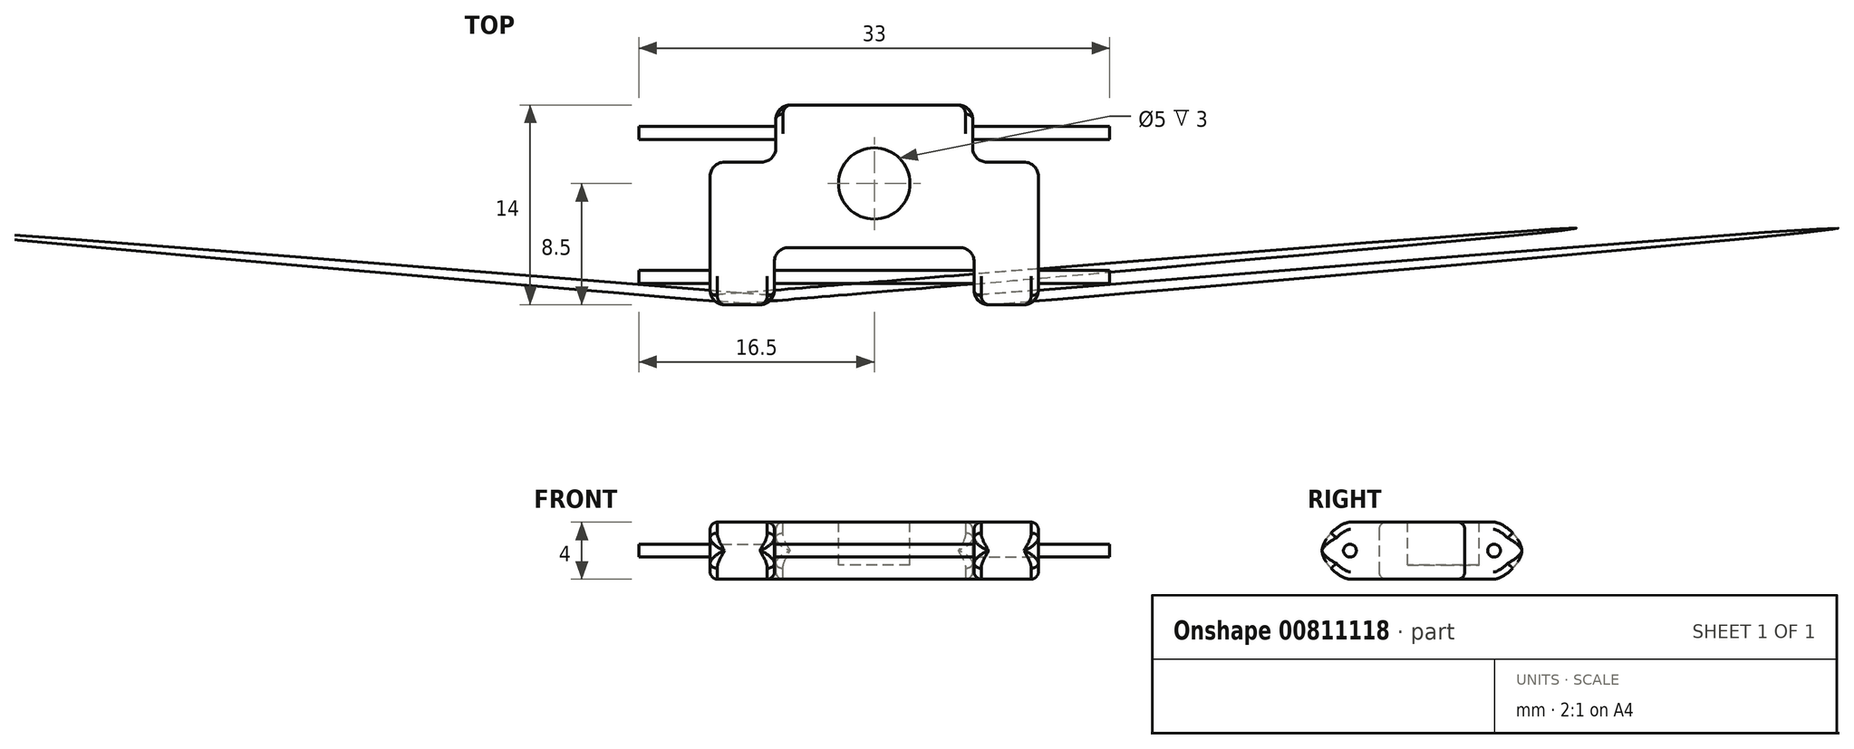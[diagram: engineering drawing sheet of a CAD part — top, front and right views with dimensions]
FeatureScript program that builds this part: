
annotation { "Feature Type Name" : "Feature", "Feature Type Description" : "" }
export const myFeature = defineFeature(function(context is Context, id is Id, definition is map)
    precondition{}
    {
        {
            var Q0;
            Q0=qCreatedBy(makeId("Top.planeOp"),FACE);
            var sketch = newSketch(context, id + "F0", { "sketchPlane" : qUnion([Q0])});
            skLineSegment(sketch, "E0", {"start": v(-1, -14) * mm, "end": v(-1, -10) * mm});
            skLineSegment(sketch, "E1", {"start": v(-1, -10) * mm, "end": v(-15, -10) * mm});
            skLineSegment(sketch, "E2", {"start": v(-15, -10) * mm, "end": v(-15, -14) * mm});
            skLineSegment(sketch, "E3", {"start": v(-15, -14) * mm, "end": v(-19.5, -14) * mm});
            skLineSegment(sketch, "E4", {"start": v(-1, -14) * mm, "end": v(3.5, -14) * mm});
            skLineSegment(sketch, "E5", {"start": v(-19.5, -14) * mm, "end": v(-19.5, -4) * mm});
            skLineSegment(sketch, "E6", {"start": v(-19.5, -4) * mm, "end": v(-14.9, -4) * mm});
            skLineSegment(sketch, "E7", {"start": v(-14.9, -4) * mm, "end": v(-14.9, 0) * mm});
            skLineSegment(sketch, "E8", {"start": v(-14.9, 0) * mm, "end": v(-1.1, 0) * mm});
            skLineSegment(sketch, "E9", {"start": v(-1.1, 0) * mm, "end": v(-1.1, -4) * mm});
            skLineSegment(sketch, "E10", {"start": v(-1.1, -4) * mm, "end": v(3.5, -4) * mm});
            skLineSegment(sketch, "E11", {"start": v(3.5, -4) * mm, "end": v(3.5, -14) * mm});
            skSolve(sketch);
        }
        {
            var Q0;
            Q0=makeQuery(id+"F0.imprint","IMPRINT",FACE,{"disambiguationData":[TD([[makeQuery(id+"F0.imprint","IMPRINT",EDGE,{"derivedFrom":sQuery(id+"F0.wireOp",EDGE,"E0")}),-1.0]])]});
            extrude(context, id + "F1", {"entities" : qUnion([Q0]), "depth" : 4 * mm, "offsetDistance" : 25 * mm});
        }
        {
            var Q0;
            Q0=makeQuery(id+"F1.opExtrude","SWEPT_EDGE",EDGE,{"disambiguationData":[OSD([sQuery(id+"F0.wireOp",EDGE,"JVpa2NSN-jCbz-SYZh-2br0-VPJ9OqO5sEDm"),sQuery(id+"F0.wireOp",EDGE,"TmuEh8Bb-qYGH-lmF9-es9h-PXmLGTj7apYS")])]});
            var Q1;
            Q1=makeQuery(id+"F1.opExtrude","SWEPT_EDGE",EDGE,{"disambiguationData":[OSD([sQuery(id+"F0.wireOp",EDGE,"Ta08JTOG-JjW1-DyQu-Rjfl-olB2hLuTZKrI"),sQuery(id+"F0.wireOp",EDGE,"5RLxsvr7-zWRq-nJ0O-23qe-XEgADmnkmLba")])]});
            var Q2;
            Q2=makeQuery(id+"F1.opExtrude","SWEPT_EDGE",EDGE,{"disambiguationData":[OSD([sQuery(id+"F0.wireOp",EDGE,"JVpa2NSN-jCbz-SYZh-2br0-VPJ9OqO5sEDm"),sQuery(id+"F0.wireOp",EDGE,"iIMMWLLX-5pRk-kAWc-YyXh-X3XYjQtiHgF8")])]});
            var Q3;
            Q3=makeQuery(id+"F1.opExtrude","SWEPT_EDGE",EDGE,{"disambiguationData":[OSD([sQuery(id+"F0.wireOp",EDGE,"Bp2VUUx9-f2Nf-Cqm2-FavC-f2X54JljXIIN"),sQuery(id+"F0.wireOp",EDGE,"TmuEh8Bb-qYGH-lmF9-es9h-PXmLGTj7apYS")])]});
            var Q4;
            Q4=makeQuery(id+"F1.opExtrude","SWEPT_EDGE",EDGE,{"disambiguationData":[OSD([sQuery(id+"F0.wireOp",EDGE,"aM0JYdi9-BpOH-c1Sx-eQZ7-4LdQcpM627Qa"),sQuery(id+"F0.wireOp",EDGE,"Ta08JTOG-JjW1-DyQu-Rjfl-olB2hLuTZKrI")])]});
            var Q5;
            Q5=makeQuery(id+"F1.opExtrude","SWEPT_EDGE",EDGE,{"disambiguationData":[OSD([sQuery(id+"F0.wireOp",EDGE,"5RLxsvr7-zWRq-nJ0O-23qe-XEgADmnkmLba"),sQuery(id+"F0.wireOp",EDGE,"Bp2VUUx9-f2Nf-Cqm2-FavC-f2X54JljXIIN")])]});
            var Q6;
            Q6=makeQuery(id+"F1.opExtrude","SWEPT_EDGE",EDGE,{"disambiguationData":[OSD([sQuery(id+"F0.wireOp",EDGE,"yeDMJLls-6pq1-5wso-vwFU-Q73Pk40JU32b"),sQuery(id+"F0.wireOp",EDGE,"aM0JYdi9-BpOH-c1Sx-eQZ7-4LdQcpM627Qa")])]});
            var Q7;
            Q7=makeQuery(id+"F1.opExtrude","SWEPT_EDGE",EDGE,{"disambiguationData":[OSD([sQuery(id+"F0.wireOp",EDGE,"yeDMJLls-6pq1-5wso-vwFU-Q73Pk40JU32b"),sQuery(id+"F0.wireOp",EDGE,"oADVPvip-QRiO-k2je-1GcM-0gCGYZzCVpqe")])]});
            var Q8;
            Q8=makeQuery(id+"F1.opExtrude","SWEPT_EDGE",EDGE,{"disambiguationData":[OSD([sQuery(id+"F0.wireOp",EDGE,"oADVPvip-QRiO-k2je-1GcM-0gCGYZzCVpqe"),sQuery(id+"F0.wireOp",EDGE,"10rlgXVg-n50c-kqx7-uExC-2RYqwfv1c7cX")])]});
            var Q9;
            Q9=makeQuery(id+"F1.opExtrude","SWEPT_EDGE",EDGE,{"disambiguationData":[OSD([sQuery(id+"F0.wireOp",EDGE,"TUznSBm0-cCe5-ovrQ-pSbA-vPagOil4q95r"),sQuery(id+"F0.wireOp",EDGE,"10rlgXVg-n50c-kqx7-uExC-2RYqwfv1c7cX")])]});
            var Q10;
            Q10=makeQuery(id+"F1.opExtrude","SWEPT_EDGE",EDGE,{"disambiguationData":[OSD([sQuery(id+"F0.wireOp",EDGE,"dIuJsfEi-w8Eu-UMFV-xWrQ-Q2fZL97E1xqK"),sQuery(id+"F0.wireOp",EDGE,"TUznSBm0-cCe5-ovrQ-pSbA-vPagOil4q95r")])]});
            var Q11;
            Q11=makeQuery(id+"F1.opExtrude","SWEPT_EDGE",EDGE,{"disambiguationData":[OSD([sQuery(id+"F0.wireOp",EDGE,"iIMMWLLX-5pRk-kAWc-YyXh-X3XYjQtiHgF8"),sQuery(id+"F0.wireOp",EDGE,"dIuJsfEi-w8Eu-UMFV-xWrQ-Q2fZL97E1xqK")])]});
            var Q12;
            Q12=makeQuery(id+"F1.opExtrude","SWEPT_EDGE",EDGE,{"disambiguationData":[OSD([sQuery(id+"F0.wireOp",EDGE,"yLF3BCVI-Jb2U-5dZP-aiB0-7200LCA53yiJ"),sQuery(id+"F0.wireOp",EDGE,"E3")])]});
            var Q13;
            Q13=makeQuery(id+"F1.opExtrude","SWEPT_EDGE",EDGE,{"disambiguationData":[OSD([sQuery(id+"F0.wireOp",EDGE,"E2"),sQuery(id+"F0.wireOp",EDGE,"E3")])]});
            var Q14;
            Q14=makeQuery(id+"F1.opExtrude","SWEPT_EDGE",EDGE,{"disambiguationData":[OSD([sQuery(id+"F0.wireOp",EDGE,"E1"),sQuery(id+"F0.wireOp",EDGE,"E2")])]});
            var Q15;
            Q15=makeQuery(id+"F1.opExtrude","SWEPT_EDGE",EDGE,{"disambiguationData":[OSD([sQuery(id+"F0.wireOp",EDGE,"E0"),sQuery(id+"F0.wireOp",EDGE,"E1")])]});
            var Q16;
            Q16=makeQuery(id+"F1.opExtrude","SWEPT_EDGE",EDGE,{"disambiguationData":[OSD([sQuery(id+"F0.wireOp",EDGE,"E0"),sQuery(id+"F0.wireOp",EDGE,"E4")])]});
            var Q17;
            Q17=makeQuery(id+"F1.opExtrude","SWEPT_EDGE",EDGE,{"disambiguationData":[OSD([sQuery(id+"F0.wireOp",EDGE,"W0sLsfjq-YAJu-qSV0-cM3q-n6XLMPe2tytr"),sQuery(id+"F0.wireOp",EDGE,"E4")])]});
            var Q18;
            Q18=makeQuery(id+"F1.opExtrude","SWEPT_EDGE",EDGE,{"disambiguationData":[OSD([sQuery(id+"F0.wireOp",EDGE,"E5"),sQuery(id+"F0.wireOp",EDGE,"E6")])]});
            var Q19;
            Q19=makeQuery(id+"F1.opExtrude","SWEPT_EDGE",EDGE,{"disambiguationData":[OSD([sQuery(id+"F0.wireOp",EDGE,"E6"),sQuery(id+"F0.wireOp",EDGE,"E7")])]});
            var Q20;
            Q20=makeQuery(id+"F1.opExtrude","SWEPT_EDGE",EDGE,{"disambiguationData":[OSD([sQuery(id+"F0.wireOp",EDGE,"E7"),sQuery(id+"F0.wireOp",EDGE,"E8")])]});
            var Q21;
            Q21=makeQuery(id+"F1.opExtrude","SWEPT_EDGE",EDGE,{"disambiguationData":[OSD([sQuery(id+"F0.wireOp",EDGE,"E8"),sQuery(id+"F0.wireOp",EDGE,"E9")])]});
            var Q22;
            Q22=makeQuery(id+"F1.opExtrude","SWEPT_EDGE",EDGE,{"disambiguationData":[OSD([sQuery(id+"F0.wireOp",EDGE,"E9"),sQuery(id+"F0.wireOp",EDGE,"E10")])]});
            var Q23;
            Q23=makeQuery(id+"F1.opExtrude","SWEPT_EDGE",EDGE,{"disambiguationData":[OSD([sQuery(id+"F0.wireOp",EDGE,"E10"),sQuery(id+"F0.wireOp",EDGE,"E11")])]});
            fillet(context, id + "F2", {"entities" : qUnion([Q0, Q1, Q2, Q3, Q4, Q5, Q6, Q7, Q8, Q9, Q10, Q11, Q12, Q13, Q14, Q15, Q16, Q17, Q18, Q19, Q20, Q21, Q22, Q23]), "radius" : 1 * mm, "tangentPropagation" : true, "allowEdgeOverflow" : false});
        }
        {
            var Q0;
            Q0=makeQuery(id+"F1.opExtrude","CAP_EDGE",EDGE,{"disambiguationData":[OSD([sQuery(id+"F0.wireOp",EDGE,"E8")])],"isStart":true});
            var Q1;
            Q1=makeQuery(id+"F1.opExtrude","CAP_EDGE",EDGE,{"disambiguationData":[OSD([sQuery(id+"F0.wireOp",EDGE,"E8")])],"isStart":false});
            var Q2;
            Q2=makeQuery(id+"F1.opExtrude","CAP_EDGE",EDGE,{"disambiguationData":[OSD([sQuery(id+"F0.wireOp",EDGE,"E3")])],"isStart":true});
            var Q3;
            Q3=makeQuery(id+"F1.opExtrude","CAP_EDGE",EDGE,{"disambiguationData":[OSD([sQuery(id+"F0.wireOp",EDGE,"E3")])],"isStart":false});
            var Q4;
            Q4=makeQuery(id+"F1.opExtrude","CAP_EDGE",EDGE,{"disambiguationData":[OSD([sQuery(id+"F0.wireOp",EDGE,"E4")])],"isStart":false});
            var Q5;
            Q5=makeQuery(id+"F1.opExtrude","CAP_EDGE",EDGE,{"disambiguationData":[OSD([sQuery(id+"F0.wireOp",EDGE,"E4")])],"isStart":true});
            fillet(context, id + "F3", {"entities" : qUnion([Q0, Q1, Q2, Q3, Q4, Q5]), "radius" : 2 * mm, "rho" : 0.3, "crossSection" : FilletCrossSection.CONIC, "allowEdgeOverflow" : false});
        }
        {
            var Q0;
            Q0=makeQuery(id+"F1.opExtrude","CAP_EDGE",EDGE,{"disambiguationData":[OSD([sQuery(id+"F0.wireOp",EDGE,"E1")])],"isStart":true});
            var Q1;
            {var subQ0=sQuery(id+"F0.wireOp",EDGE,"E2");var subQ1=sQuery(id+"F0.wireOp",EDGE,"E1");Q1=makeQuery(id+"F2.opFillet","BLEND_EDGE",EDGE,{"blendedFrom":[makeQuery(id+"F1.opExtrude","SWEPT_EDGE",EDGE,{"disambiguationData":[OSD([subQ1,subQ0])]}),makeQuery(id+"F1.opExtrude","CAP_FACE",FACE,{"disambiguationData":[OSD([sQuery(id+"F0.wireOp",EDGE,"E0"),subQ1,subQ0,sQuery(id+"F0.wireOp",EDGE,"E3"),sQuery(id+"F0.wireOp",EDGE,"E4"),sQuery(id+"F0.wireOp",EDGE,"E5"),sQuery(id+"F0.wireOp",EDGE,"E6"),sQuery(id+"F0.wireOp",EDGE,"E7"),sQuery(id+"F0.wireOp",EDGE,"E8"),sQuery(id+"F0.wireOp",EDGE,"E9"),sQuery(id+"F0.wireOp",EDGE,"E10"),sQuery(id+"F0.wireOp",EDGE,"E11")])],"isStart":true})],"blendedInto":[makeQuery(id+"F1.opExtrude","CAP_FACE",FACE,{"disambiguationData":[OSD([sQuery(id+"F0.wireOp",EDGE,"E0"),subQ1,subQ0,sQuery(id+"F0.wireOp",EDGE,"E3"),sQuery(id+"F0.wireOp",EDGE,"E4"),sQuery(id+"F0.wireOp",EDGE,"E5"),sQuery(id+"F0.wireOp",EDGE,"E6"),sQuery(id+"F0.wireOp",EDGE,"E7"),sQuery(id+"F0.wireOp",EDGE,"E8"),sQuery(id+"F0.wireOp",EDGE,"E9"),sQuery(id+"F0.wireOp",EDGE,"E10"),sQuery(id+"F0.wireOp",EDGE,"E11")])],"isStart":true})]});}
            var Q2;
            Q2=makeQuery(id+"F1.opExtrude","CAP_EDGE",EDGE,{"disambiguationData":[OSD([sQuery(id+"F0.wireOp",EDGE,"E2")])],"isStart":true});
            var Q3;
            Q3=makeQuery(id+"F3.opFillet","BLEND_EDGE",EDGE,{"blendedFrom":[makeQuery(id+"F1.opExtrude","CAP_EDGE",EDGE,{"disambiguationData":[OSD([sQuery(id+"F0.wireOp",EDGE,"E3")])],"isStart":true}),makeQuery(id+"F1.opExtrude","SWEPT_FACE",FACE,{"disambiguationData":[OSD([sQuery(id+"F0.wireOp",EDGE,"E2")])]})],"blendedInto":[makeQuery(id+"F1.opExtrude","SWEPT_FACE",FACE,{"disambiguationData":[OSD([sQuery(id+"F0.wireOp",EDGE,"E2")])]})]});
            var Q4;
            {var subQ0=sQuery(id+"F0.wireOp",EDGE,"E3");Q4=makeQuery(id+"F3.opFillet","BLEND_EDGE",EDGE,{"blendedFrom":[makeQuery(id+"F1.opExtrude","CAP_EDGE",EDGE,{"disambiguationData":[OSD([subQ0])],"isStart":true}),makeQuery(id+"F2.opFillet","BLEND_FACE",FACE,{"disambiguationData":[OSD([sQuery(id+"F0.wireOp",EDGE,"E2"),subQ0])]})],"blendedInto":[makeQuery(id+"F2.opFillet","BLEND_FACE",FACE,{"disambiguationData":[OSD([sQuery(id+"F0.wireOp",EDGE,"E2"),subQ0])]})]});}
            var Q5;
            {var subQ0=sQuery(id+"F0.wireOp",EDGE,"E1");var subQ1=sQuery(id+"F0.wireOp",EDGE,"E0");Q5=makeQuery(id+"F2.opFillet","BLEND_EDGE",EDGE,{"blendedFrom":[makeQuery(id+"F1.opExtrude","SWEPT_EDGE",EDGE,{"disambiguationData":[OSD([subQ1,subQ0])]}),makeQuery(id+"F1.opExtrude","CAP_FACE",FACE,{"disambiguationData":[OSD([subQ1,subQ0,sQuery(id+"F0.wireOp",EDGE,"E2"),sQuery(id+"F0.wireOp",EDGE,"E3"),sQuery(id+"F0.wireOp",EDGE,"E4"),sQuery(id+"F0.wireOp",EDGE,"E5"),sQuery(id+"F0.wireOp",EDGE,"E6"),sQuery(id+"F0.wireOp",EDGE,"E7"),sQuery(id+"F0.wireOp",EDGE,"E8"),sQuery(id+"F0.wireOp",EDGE,"E9"),sQuery(id+"F0.wireOp",EDGE,"E10"),sQuery(id+"F0.wireOp",EDGE,"E11")])],"isStart":true})],"blendedInto":[makeQuery(id+"F1.opExtrude","CAP_FACE",FACE,{"disambiguationData":[OSD([subQ1,subQ0,sQuery(id+"F0.wireOp",EDGE,"E2"),sQuery(id+"F0.wireOp",EDGE,"E3"),sQuery(id+"F0.wireOp",EDGE,"E4"),sQuery(id+"F0.wireOp",EDGE,"E5"),sQuery(id+"F0.wireOp",EDGE,"E6"),sQuery(id+"F0.wireOp",EDGE,"E7"),sQuery(id+"F0.wireOp",EDGE,"E8"),sQuery(id+"F0.wireOp",EDGE,"E9"),sQuery(id+"F0.wireOp",EDGE,"E10"),sQuery(id+"F0.wireOp",EDGE,"E11")])],"isStart":true})]});}
            var Q6;
            Q6=makeQuery(id+"F1.opExtrude","CAP_EDGE",EDGE,{"disambiguationData":[OSD([sQuery(id+"F0.wireOp",EDGE,"E0")])],"isStart":true});
            var Q7;
            {var subQ0=sQuery(id+"F0.wireOp",EDGE,"E4");Q7=makeQuery(id+"F3.opFillet","BLEND_EDGE",EDGE,{"blendedFrom":[makeQuery(id+"F1.opExtrude","CAP_EDGE",EDGE,{"disambiguationData":[OSD([subQ0])],"isStart":true}),makeQuery(id+"F2.opFillet","BLEND_FACE",FACE,{"disambiguationData":[OSD([sQuery(id+"F0.wireOp",EDGE,"E0"),subQ0])]})],"blendedInto":[makeQuery(id+"F2.opFillet","BLEND_FACE",FACE,{"disambiguationData":[OSD([sQuery(id+"F0.wireOp",EDGE,"E0"),subQ0])]})]});}
            var Q8;
            {var subQ0=sQuery(id+"F0.wireOp",EDGE,"E4");Q8=makeQuery(id+"F3.opFillet","BLEND_EDGE",EDGE,{"blendedFrom":[makeQuery(id+"F1.opExtrude","CAP_EDGE",EDGE,{"disambiguationData":[OSD([subQ0])],"isStart":false}),makeQuery(id+"F2.opFillet","BLEND_FACE",FACE,{"disambiguationData":[OSD([sQuery(id+"F0.wireOp",EDGE,"E0"),subQ0])]})],"blendedInto":[makeQuery(id+"F2.opFillet","BLEND_FACE",FACE,{"disambiguationData":[OSD([sQuery(id+"F0.wireOp",EDGE,"E0"),subQ0])]})]});}
            var Q9;
            {var subQ0=sQuery(id+"F0.wireOp",EDGE,"E3");Q9=makeQuery(id+"F3.opFillet","BLEND_EDGE",EDGE,{"blendedFrom":[makeQuery(id+"F1.opExtrude","CAP_EDGE",EDGE,{"disambiguationData":[OSD([subQ0])],"isStart":false}),makeQuery(id+"F2.opFillet","BLEND_FACE",FACE,{"disambiguationData":[OSD([sQuery(id+"F0.wireOp",EDGE,"E2"),subQ0])]})],"blendedInto":[makeQuery(id+"F2.opFillet","BLEND_FACE",FACE,{"disambiguationData":[OSD([sQuery(id+"F0.wireOp",EDGE,"E2"),subQ0])]})]});}
            var Q10;
            Q10=makeQuery(id+"F3.opFillet","BLEND_EDGE",EDGE,{"blendedFrom":[makeQuery(id+"F1.opExtrude","CAP_EDGE",EDGE,{"disambiguationData":[OSD([sQuery(id+"F0.wireOp",EDGE,"E3")])],"isStart":false}),makeQuery(id+"F1.opExtrude","SWEPT_FACE",FACE,{"disambiguationData":[OSD([sQuery(id+"F0.wireOp",EDGE,"E2")])]})],"blendedInto":[makeQuery(id+"F1.opExtrude","SWEPT_FACE",FACE,{"disambiguationData":[OSD([sQuery(id+"F0.wireOp",EDGE,"E2")])]})]});
            var Q11;
            Q11=makeQuery(id+"F1.opExtrude","CAP_EDGE",EDGE,{"disambiguationData":[OSD([sQuery(id+"F0.wireOp",EDGE,"E2")])],"isStart":false});
            var Q12;
            {var subQ0=sQuery(id+"F0.wireOp",EDGE,"E2");var subQ1=sQuery(id+"F0.wireOp",EDGE,"E1");Q12=makeQuery(id+"F2.opFillet","BLEND_EDGE",EDGE,{"blendedFrom":[makeQuery(id+"F1.opExtrude","SWEPT_EDGE",EDGE,{"disambiguationData":[OSD([subQ1,subQ0])]}),makeQuery(id+"F1.opExtrude","CAP_FACE",FACE,{"disambiguationData":[OSD([sQuery(id+"F0.wireOp",EDGE,"E0"),subQ1,subQ0,sQuery(id+"F0.wireOp",EDGE,"E3"),sQuery(id+"F0.wireOp",EDGE,"E4"),sQuery(id+"F0.wireOp",EDGE,"E5"),sQuery(id+"F0.wireOp",EDGE,"E6"),sQuery(id+"F0.wireOp",EDGE,"E7"),sQuery(id+"F0.wireOp",EDGE,"E8"),sQuery(id+"F0.wireOp",EDGE,"E9"),sQuery(id+"F0.wireOp",EDGE,"E10"),sQuery(id+"F0.wireOp",EDGE,"E11")])],"isStart":false})],"blendedInto":[makeQuery(id+"F1.opExtrude","CAP_FACE",FACE,{"disambiguationData":[OSD([sQuery(id+"F0.wireOp",EDGE,"E0"),subQ1,subQ0,sQuery(id+"F0.wireOp",EDGE,"E3"),sQuery(id+"F0.wireOp",EDGE,"E4"),sQuery(id+"F0.wireOp",EDGE,"E5"),sQuery(id+"F0.wireOp",EDGE,"E6"),sQuery(id+"F0.wireOp",EDGE,"E7"),sQuery(id+"F0.wireOp",EDGE,"E8"),sQuery(id+"F0.wireOp",EDGE,"E9"),sQuery(id+"F0.wireOp",EDGE,"E10"),sQuery(id+"F0.wireOp",EDGE,"E11")])],"isStart":false})]});}
            var Q13;
            Q13=makeQuery(id+"F1.opExtrude","CAP_EDGE",EDGE,{"disambiguationData":[OSD([sQuery(id+"F0.wireOp",EDGE,"E1")])],"isStart":false});
            var Q14;
            {var subQ0=sQuery(id+"F0.wireOp",EDGE,"E1");var subQ1=sQuery(id+"F0.wireOp",EDGE,"E0");Q14=makeQuery(id+"F2.opFillet","BLEND_EDGE",EDGE,{"blendedFrom":[makeQuery(id+"F1.opExtrude","SWEPT_EDGE",EDGE,{"disambiguationData":[OSD([subQ1,subQ0])]}),makeQuery(id+"F1.opExtrude","CAP_FACE",FACE,{"disambiguationData":[OSD([subQ1,subQ0,sQuery(id+"F0.wireOp",EDGE,"E2"),sQuery(id+"F0.wireOp",EDGE,"E3"),sQuery(id+"F0.wireOp",EDGE,"E4"),sQuery(id+"F0.wireOp",EDGE,"E5"),sQuery(id+"F0.wireOp",EDGE,"E6"),sQuery(id+"F0.wireOp",EDGE,"E7"),sQuery(id+"F0.wireOp",EDGE,"E8"),sQuery(id+"F0.wireOp",EDGE,"E9"),sQuery(id+"F0.wireOp",EDGE,"E10"),sQuery(id+"F0.wireOp",EDGE,"E11")])],"isStart":false})],"blendedInto":[makeQuery(id+"F1.opExtrude","CAP_FACE",FACE,{"disambiguationData":[OSD([subQ1,subQ0,sQuery(id+"F0.wireOp",EDGE,"E2"),sQuery(id+"F0.wireOp",EDGE,"E3"),sQuery(id+"F0.wireOp",EDGE,"E4"),sQuery(id+"F0.wireOp",EDGE,"E5"),sQuery(id+"F0.wireOp",EDGE,"E6"),sQuery(id+"F0.wireOp",EDGE,"E7"),sQuery(id+"F0.wireOp",EDGE,"E8"),sQuery(id+"F0.wireOp",EDGE,"E9"),sQuery(id+"F0.wireOp",EDGE,"E10"),sQuery(id+"F0.wireOp",EDGE,"E11")])],"isStart":false})]});}
            var Q15;
            Q15=makeQuery(id+"F1.opExtrude","CAP_EDGE",EDGE,{"disambiguationData":[OSD([sQuery(id+"F0.wireOp",EDGE,"E0")])],"isStart":false});
            var Q16;
            Q16=makeQuery(id+"F3.opFillet","BLEND_EDGE",EDGE,{"blendedFrom":[makeQuery(id+"F1.opExtrude","CAP_EDGE",EDGE,{"disambiguationData":[OSD([sQuery(id+"F0.wireOp",EDGE,"E4")])],"isStart":false}),makeQuery(id+"F1.opExtrude","SWEPT_FACE",FACE,{"disambiguationData":[OSD([sQuery(id+"F0.wireOp",EDGE,"E0")])]})],"blendedInto":[makeQuery(id+"F1.opExtrude","SWEPT_FACE",FACE,{"disambiguationData":[OSD([sQuery(id+"F0.wireOp",EDGE,"E0")])]})]});
            var Q17;
            Q17=makeQuery(id+"F3.opFillet","BLEND_EDGE",EDGE,{"blendedFrom":[makeQuery(id+"F1.opExtrude","CAP_EDGE",EDGE,{"disambiguationData":[OSD([sQuery(id+"F0.wireOp",EDGE,"E4")])],"isStart":true}),makeQuery(id+"F1.opExtrude","SWEPT_FACE",FACE,{"disambiguationData":[OSD([sQuery(id+"F0.wireOp",EDGE,"E0")])]})],"blendedInto":[makeQuery(id+"F1.opExtrude","SWEPT_FACE",FACE,{"disambiguationData":[OSD([sQuery(id+"F0.wireOp",EDGE,"E0")])]})]});
            var Q18;
            {var subQ0=sQuery(id+"F0.wireOp",EDGE,"E3");Q18=makeQuery(id+"F3.opFillet","BLEND_EDGE",EDGE,{"blendedFrom":[makeQuery(id+"F1.opExtrude","CAP_EDGE",EDGE,{"disambiguationData":[OSD([subQ0])],"isStart":false}),makeQuery(id+"F2.opFillet","BLEND_FACE",FACE,{"disambiguationData":[OSD([subQ0,sQuery(id+"F0.wireOp",EDGE,"E5")])]})],"blendedInto":[makeQuery(id+"F2.opFillet","BLEND_FACE",FACE,{"disambiguationData":[OSD([subQ0,sQuery(id+"F0.wireOp",EDGE,"E5")])]})]});}
            var Q19;
            {var subQ0=sQuery(id+"F0.wireOp",EDGE,"E3");Q19=makeQuery(id+"F3.opFillet","BLEND_EDGE",EDGE,{"blendedFrom":[makeQuery(id+"F1.opExtrude","CAP_EDGE",EDGE,{"disambiguationData":[OSD([subQ0])],"isStart":true}),makeQuery(id+"F2.opFillet","BLEND_FACE",FACE,{"disambiguationData":[OSD([subQ0,sQuery(id+"F0.wireOp",EDGE,"E5")])]})],"blendedInto":[makeQuery(id+"F2.opFillet","BLEND_FACE",FACE,{"disambiguationData":[OSD([subQ0,sQuery(id+"F0.wireOp",EDGE,"E5")])]})]});}
            var Q20;
            Q20=makeQuery(id+"F1.opExtrude","CAP_EDGE",EDGE,{"disambiguationData":[OSD([sQuery(id+"F0.wireOp",EDGE,"E5")])],"isStart":true});
            var Q21;
            Q21=makeQuery(id+"F3.opFillet","BLEND_EDGE",EDGE,{"blendedFrom":[makeQuery(id+"F1.opExtrude","CAP_EDGE",EDGE,{"disambiguationData":[OSD([sQuery(id+"F0.wireOp",EDGE,"E3")])],"isStart":true}),makeQuery(id+"F1.opExtrude","SWEPT_FACE",FACE,{"disambiguationData":[OSD([sQuery(id+"F0.wireOp",EDGE,"E5")])]})],"blendedInto":[makeQuery(id+"F1.opExtrude","SWEPT_FACE",FACE,{"disambiguationData":[OSD([sQuery(id+"F0.wireOp",EDGE,"E5")])]})]});
            var Q22;
            Q22=makeQuery(id+"F3.opFillet","BLEND_EDGE",EDGE,{"blendedFrom":[makeQuery(id+"F1.opExtrude","CAP_EDGE",EDGE,{"disambiguationData":[OSD([sQuery(id+"F0.wireOp",EDGE,"E3")])],"isStart":false}),makeQuery(id+"F1.opExtrude","SWEPT_FACE",FACE,{"disambiguationData":[OSD([sQuery(id+"F0.wireOp",EDGE,"E5")])]})],"blendedInto":[makeQuery(id+"F1.opExtrude","SWEPT_FACE",FACE,{"disambiguationData":[OSD([sQuery(id+"F0.wireOp",EDGE,"E5")])]})]});
            var Q23;
            Q23=makeQuery(id+"F1.opExtrude","CAP_EDGE",EDGE,{"disambiguationData":[OSD([sQuery(id+"F0.wireOp",EDGE,"E5")])],"isStart":false});
            var Q24;
            {var subQ0=sQuery(id+"F0.wireOp",EDGE,"E6");var subQ1=sQuery(id+"F0.wireOp",EDGE,"E5");Q24=makeQuery(id+"F2.opFillet","BLEND_EDGE",EDGE,{"blendedFrom":[makeQuery(id+"F1.opExtrude","SWEPT_EDGE",EDGE,{"disambiguationData":[OSD([subQ1,subQ0])]}),makeQuery(id+"F1.opExtrude","CAP_FACE",FACE,{"disambiguationData":[OSD([sQuery(id+"F0.wireOp",EDGE,"E0"),sQuery(id+"F0.wireOp",EDGE,"E1"),sQuery(id+"F0.wireOp",EDGE,"E2"),sQuery(id+"F0.wireOp",EDGE,"E3"),sQuery(id+"F0.wireOp",EDGE,"E4"),subQ1,subQ0,sQuery(id+"F0.wireOp",EDGE,"E7"),sQuery(id+"F0.wireOp",EDGE,"E8"),sQuery(id+"F0.wireOp",EDGE,"E9"),sQuery(id+"F0.wireOp",EDGE,"E10"),sQuery(id+"F0.wireOp",EDGE,"E11")])],"isStart":false})],"blendedInto":[makeQuery(id+"F1.opExtrude","CAP_FACE",FACE,{"disambiguationData":[OSD([sQuery(id+"F0.wireOp",EDGE,"E0"),sQuery(id+"F0.wireOp",EDGE,"E1"),sQuery(id+"F0.wireOp",EDGE,"E2"),sQuery(id+"F0.wireOp",EDGE,"E3"),sQuery(id+"F0.wireOp",EDGE,"E4"),subQ1,subQ0,sQuery(id+"F0.wireOp",EDGE,"E7"),sQuery(id+"F0.wireOp",EDGE,"E8"),sQuery(id+"F0.wireOp",EDGE,"E9"),sQuery(id+"F0.wireOp",EDGE,"E10"),sQuery(id+"F0.wireOp",EDGE,"E11")])],"isStart":false})]});}
            var Q25;
            {var subQ0=sQuery(id+"F0.wireOp",EDGE,"E6");var subQ1=sQuery(id+"F0.wireOp",EDGE,"E5");Q25=makeQuery(id+"F2.opFillet","BLEND_EDGE",EDGE,{"blendedFrom":[makeQuery(id+"F1.opExtrude","SWEPT_EDGE",EDGE,{"disambiguationData":[OSD([subQ1,subQ0])]}),makeQuery(id+"F1.opExtrude","CAP_FACE",FACE,{"disambiguationData":[OSD([sQuery(id+"F0.wireOp",EDGE,"E0"),sQuery(id+"F0.wireOp",EDGE,"E1"),sQuery(id+"F0.wireOp",EDGE,"E2"),sQuery(id+"F0.wireOp",EDGE,"E3"),sQuery(id+"F0.wireOp",EDGE,"E4"),subQ1,subQ0,sQuery(id+"F0.wireOp",EDGE,"E7"),sQuery(id+"F0.wireOp",EDGE,"E8"),sQuery(id+"F0.wireOp",EDGE,"E9"),sQuery(id+"F0.wireOp",EDGE,"E10"),sQuery(id+"F0.wireOp",EDGE,"E11")])],"isStart":true})],"blendedInto":[makeQuery(id+"F1.opExtrude","CAP_FACE",FACE,{"disambiguationData":[OSD([sQuery(id+"F0.wireOp",EDGE,"E0"),sQuery(id+"F0.wireOp",EDGE,"E1"),sQuery(id+"F0.wireOp",EDGE,"E2"),sQuery(id+"F0.wireOp",EDGE,"E3"),sQuery(id+"F0.wireOp",EDGE,"E4"),subQ1,subQ0,sQuery(id+"F0.wireOp",EDGE,"E7"),sQuery(id+"F0.wireOp",EDGE,"E8"),sQuery(id+"F0.wireOp",EDGE,"E9"),sQuery(id+"F0.wireOp",EDGE,"E10"),sQuery(id+"F0.wireOp",EDGE,"E11")])],"isStart":true})]});}
            var Q26;
            Q26=makeQuery(id+"F1.opExtrude","CAP_EDGE",EDGE,{"disambiguationData":[OSD([sQuery(id+"F0.wireOp",EDGE,"E6")])],"isStart":true});
            var Q27;
            Q27=makeQuery(id+"F1.opExtrude","CAP_EDGE",EDGE,{"disambiguationData":[OSD([sQuery(id+"F0.wireOp",EDGE,"E6")])],"isStart":false});
            var Q28;
            {var subQ0=sQuery(id+"F0.wireOp",EDGE,"E7");var subQ1=sQuery(id+"F0.wireOp",EDGE,"E6");Q28=makeQuery(id+"F2.opFillet","BLEND_EDGE",EDGE,{"blendedFrom":[makeQuery(id+"F1.opExtrude","SWEPT_EDGE",EDGE,{"disambiguationData":[OSD([subQ1,subQ0])]}),makeQuery(id+"F1.opExtrude","CAP_FACE",FACE,{"disambiguationData":[OSD([sQuery(id+"F0.wireOp",EDGE,"E0"),sQuery(id+"F0.wireOp",EDGE,"E1"),sQuery(id+"F0.wireOp",EDGE,"E2"),sQuery(id+"F0.wireOp",EDGE,"E3"),sQuery(id+"F0.wireOp",EDGE,"E4"),sQuery(id+"F0.wireOp",EDGE,"E5"),subQ1,subQ0,sQuery(id+"F0.wireOp",EDGE,"E8"),sQuery(id+"F0.wireOp",EDGE,"E9"),sQuery(id+"F0.wireOp",EDGE,"E10"),sQuery(id+"F0.wireOp",EDGE,"E11")])],"isStart":false})],"blendedInto":[makeQuery(id+"F1.opExtrude","CAP_FACE",FACE,{"disambiguationData":[OSD([sQuery(id+"F0.wireOp",EDGE,"E0"),sQuery(id+"F0.wireOp",EDGE,"E1"),sQuery(id+"F0.wireOp",EDGE,"E2"),sQuery(id+"F0.wireOp",EDGE,"E3"),sQuery(id+"F0.wireOp",EDGE,"E4"),sQuery(id+"F0.wireOp",EDGE,"E5"),subQ1,subQ0,sQuery(id+"F0.wireOp",EDGE,"E8"),sQuery(id+"F0.wireOp",EDGE,"E9"),sQuery(id+"F0.wireOp",EDGE,"E10"),sQuery(id+"F0.wireOp",EDGE,"E11")])],"isStart":false})]});}
            var Q29;
            {var subQ0=sQuery(id+"F0.wireOp",EDGE,"E7");var subQ1=sQuery(id+"F0.wireOp",EDGE,"E6");Q29=makeQuery(id+"F2.opFillet","BLEND_EDGE",EDGE,{"blendedFrom":[makeQuery(id+"F1.opExtrude","SWEPT_EDGE",EDGE,{"disambiguationData":[OSD([subQ1,subQ0])]}),makeQuery(id+"F1.opExtrude","CAP_FACE",FACE,{"disambiguationData":[OSD([sQuery(id+"F0.wireOp",EDGE,"E0"),sQuery(id+"F0.wireOp",EDGE,"E1"),sQuery(id+"F0.wireOp",EDGE,"E2"),sQuery(id+"F0.wireOp",EDGE,"E3"),sQuery(id+"F0.wireOp",EDGE,"E4"),sQuery(id+"F0.wireOp",EDGE,"E5"),subQ1,subQ0,sQuery(id+"F0.wireOp",EDGE,"E8"),sQuery(id+"F0.wireOp",EDGE,"E9"),sQuery(id+"F0.wireOp",EDGE,"E10"),sQuery(id+"F0.wireOp",EDGE,"E11")])],"isStart":true})],"blendedInto":[makeQuery(id+"F1.opExtrude","CAP_FACE",FACE,{"disambiguationData":[OSD([sQuery(id+"F0.wireOp",EDGE,"E0"),sQuery(id+"F0.wireOp",EDGE,"E1"),sQuery(id+"F0.wireOp",EDGE,"E2"),sQuery(id+"F0.wireOp",EDGE,"E3"),sQuery(id+"F0.wireOp",EDGE,"E4"),sQuery(id+"F0.wireOp",EDGE,"E5"),subQ1,subQ0,sQuery(id+"F0.wireOp",EDGE,"E8"),sQuery(id+"F0.wireOp",EDGE,"E9"),sQuery(id+"F0.wireOp",EDGE,"E10"),sQuery(id+"F0.wireOp",EDGE,"E11")])],"isStart":true})]});}
            var Q30;
            Q30=makeQuery(id+"F3.opFillet","BLEND_EDGE",EDGE,{"blendedFrom":[makeQuery(id+"F1.opExtrude","CAP_EDGE",EDGE,{"disambiguationData":[OSD([sQuery(id+"F0.wireOp",EDGE,"E8")])],"isStart":false}),makeQuery(id+"F1.opExtrude","SWEPT_FACE",FACE,{"disambiguationData":[OSD([sQuery(id+"F0.wireOp",EDGE,"E7")])]})],"blendedInto":[makeQuery(id+"F1.opExtrude","SWEPT_FACE",FACE,{"disambiguationData":[OSD([sQuery(id+"F0.wireOp",EDGE,"E7")])]})]});
            var Q31;
            Q31=makeQuery(id+"F1.opExtrude","CAP_EDGE",EDGE,{"disambiguationData":[OSD([sQuery(id+"F0.wireOp",EDGE,"E7")])],"isStart":false});
            var Q32;
            {var subQ0=sQuery(id+"F0.wireOp",EDGE,"E8");Q32=makeQuery(id+"F3.opFillet","BLEND_EDGE",EDGE,{"blendedFrom":[makeQuery(id+"F1.opExtrude","CAP_EDGE",EDGE,{"disambiguationData":[OSD([subQ0])],"isStart":false}),makeQuery(id+"F2.opFillet","BLEND_FACE",FACE,{"disambiguationData":[OSD([sQuery(id+"F0.wireOp",EDGE,"E7"),subQ0])]})],"blendedInto":[makeQuery(id+"F2.opFillet","BLEND_FACE",FACE,{"disambiguationData":[OSD([sQuery(id+"F0.wireOp",EDGE,"E7"),subQ0])]})]});}
            var Q33;
            {var subQ0=sQuery(id+"F0.wireOp",EDGE,"E8");Q33=makeQuery(id+"F3.opFillet","BLEND_EDGE",EDGE,{"blendedFrom":[makeQuery(id+"F1.opExtrude","CAP_EDGE",EDGE,{"disambiguationData":[OSD([subQ0])],"isStart":true}),makeQuery(id+"F2.opFillet","BLEND_FACE",FACE,{"disambiguationData":[OSD([sQuery(id+"F0.wireOp",EDGE,"E7"),subQ0])]})],"blendedInto":[makeQuery(id+"F2.opFillet","BLEND_FACE",FACE,{"disambiguationData":[OSD([sQuery(id+"F0.wireOp",EDGE,"E7"),subQ0])]})]});}
            var Q34;
            Q34=makeQuery(id+"F3.opFillet","BLEND_EDGE",EDGE,{"blendedFrom":[makeQuery(id+"F1.opExtrude","CAP_EDGE",EDGE,{"disambiguationData":[OSD([sQuery(id+"F0.wireOp",EDGE,"E8")])],"isStart":true}),makeQuery(id+"F1.opExtrude","SWEPT_FACE",FACE,{"disambiguationData":[OSD([sQuery(id+"F0.wireOp",EDGE,"E7")])]})],"blendedInto":[makeQuery(id+"F1.opExtrude","SWEPT_FACE",FACE,{"disambiguationData":[OSD([sQuery(id+"F0.wireOp",EDGE,"E7")])]})]});
            var Q35;
            Q35=makeQuery(id+"F1.opExtrude","CAP_EDGE",EDGE,{"disambiguationData":[OSD([sQuery(id+"F0.wireOp",EDGE,"E7")])],"isStart":true});
            var Q36;
            {var subQ0=sQuery(id+"F0.wireOp",EDGE,"E8");Q36=makeQuery(id+"F3.opFillet","BLEND_EDGE",EDGE,{"blendedFrom":[makeQuery(id+"F1.opExtrude","CAP_EDGE",EDGE,{"disambiguationData":[OSD([subQ0])],"isStart":true}),makeQuery(id+"F2.opFillet","BLEND_FACE",FACE,{"disambiguationData":[OSD([subQ0,sQuery(id+"F0.wireOp",EDGE,"E9")])]})],"blendedInto":[makeQuery(id+"F2.opFillet","BLEND_FACE",FACE,{"disambiguationData":[OSD([subQ0,sQuery(id+"F0.wireOp",EDGE,"E9")])]})]});}
            var Q37;
            Q37=makeQuery(id+"F3.opFillet","BLEND_EDGE",EDGE,{"blendedFrom":[makeQuery(id+"F1.opExtrude","CAP_EDGE",EDGE,{"disambiguationData":[OSD([sQuery(id+"F0.wireOp",EDGE,"E8")])],"isStart":true}),makeQuery(id+"F1.opExtrude","SWEPT_FACE",FACE,{"disambiguationData":[OSD([sQuery(id+"F0.wireOp",EDGE,"E9")])]})],"blendedInto":[makeQuery(id+"F1.opExtrude","SWEPT_FACE",FACE,{"disambiguationData":[OSD([sQuery(id+"F0.wireOp",EDGE,"E9")])]})]});
            var Q38;
            Q38=makeQuery(id+"F1.opExtrude","CAP_EDGE",EDGE,{"disambiguationData":[OSD([sQuery(id+"F0.wireOp",EDGE,"E9")])],"isStart":true});
            var Q39;
            {var subQ0=sQuery(id+"F0.wireOp",EDGE,"E10");var subQ1=sQuery(id+"F0.wireOp",EDGE,"E9");Q39=makeQuery(id+"F2.opFillet","BLEND_EDGE",EDGE,{"blendedFrom":[makeQuery(id+"F1.opExtrude","SWEPT_EDGE",EDGE,{"disambiguationData":[OSD([subQ1,subQ0])]}),makeQuery(id+"F1.opExtrude","CAP_FACE",FACE,{"disambiguationData":[OSD([sQuery(id+"F0.wireOp",EDGE,"E0"),sQuery(id+"F0.wireOp",EDGE,"E1"),sQuery(id+"F0.wireOp",EDGE,"E2"),sQuery(id+"F0.wireOp",EDGE,"E3"),sQuery(id+"F0.wireOp",EDGE,"E4"),sQuery(id+"F0.wireOp",EDGE,"E5"),sQuery(id+"F0.wireOp",EDGE,"E6"),sQuery(id+"F0.wireOp",EDGE,"E7"),sQuery(id+"F0.wireOp",EDGE,"E8"),subQ1,subQ0,sQuery(id+"F0.wireOp",EDGE,"E11")])],"isStart":true})],"blendedInto":[makeQuery(id+"F1.opExtrude","CAP_FACE",FACE,{"disambiguationData":[OSD([sQuery(id+"F0.wireOp",EDGE,"E0"),sQuery(id+"F0.wireOp",EDGE,"E1"),sQuery(id+"F0.wireOp",EDGE,"E2"),sQuery(id+"F0.wireOp",EDGE,"E3"),sQuery(id+"F0.wireOp",EDGE,"E4"),sQuery(id+"F0.wireOp",EDGE,"E5"),sQuery(id+"F0.wireOp",EDGE,"E6"),sQuery(id+"F0.wireOp",EDGE,"E7"),sQuery(id+"F0.wireOp",EDGE,"E8"),subQ1,subQ0,sQuery(id+"F0.wireOp",EDGE,"E11")])],"isStart":true})]});}
            var Q40;
            Q40=makeQuery(id+"F1.opExtrude","CAP_EDGE",EDGE,{"disambiguationData":[OSD([sQuery(id+"F0.wireOp",EDGE,"E10")])],"isStart":true});
            var Q41;
            {var subQ0=sQuery(id+"F0.wireOp",EDGE,"E11");var subQ1=sQuery(id+"F0.wireOp",EDGE,"E10");Q41=makeQuery(id+"F2.opFillet","BLEND_EDGE",EDGE,{"blendedFrom":[makeQuery(id+"F1.opExtrude","SWEPT_EDGE",EDGE,{"disambiguationData":[OSD([subQ1,subQ0])]}),makeQuery(id+"F1.opExtrude","CAP_FACE",FACE,{"disambiguationData":[OSD([sQuery(id+"F0.wireOp",EDGE,"E0"),sQuery(id+"F0.wireOp",EDGE,"E1"),sQuery(id+"F0.wireOp",EDGE,"E2"),sQuery(id+"F0.wireOp",EDGE,"E3"),sQuery(id+"F0.wireOp",EDGE,"E4"),sQuery(id+"F0.wireOp",EDGE,"E5"),sQuery(id+"F0.wireOp",EDGE,"E6"),sQuery(id+"F0.wireOp",EDGE,"E7"),sQuery(id+"F0.wireOp",EDGE,"E8"),sQuery(id+"F0.wireOp",EDGE,"E9"),subQ1,subQ0])],"isStart":true})],"blendedInto":[makeQuery(id+"F1.opExtrude","CAP_FACE",FACE,{"disambiguationData":[OSD([sQuery(id+"F0.wireOp",EDGE,"E0"),sQuery(id+"F0.wireOp",EDGE,"E1"),sQuery(id+"F0.wireOp",EDGE,"E2"),sQuery(id+"F0.wireOp",EDGE,"E3"),sQuery(id+"F0.wireOp",EDGE,"E4"),sQuery(id+"F0.wireOp",EDGE,"E5"),sQuery(id+"F0.wireOp",EDGE,"E6"),sQuery(id+"F0.wireOp",EDGE,"E7"),sQuery(id+"F0.wireOp",EDGE,"E8"),sQuery(id+"F0.wireOp",EDGE,"E9"),subQ1,subQ0])],"isStart":true})]});}
            var Q42;
            Q42=makeQuery(id+"F1.opExtrude","CAP_EDGE",EDGE,{"disambiguationData":[OSD([sQuery(id+"F0.wireOp",EDGE,"E11")])],"isStart":true});
            var Q43;
            Q43=makeQuery(id+"F1.opExtrude","CAP_EDGE",EDGE,{"disambiguationData":[OSD([sQuery(id+"F0.wireOp",EDGE,"E11")])],"isStart":false});
            var Q44;
            {var subQ0=sQuery(id+"F0.wireOp",EDGE,"E11");var subQ1=sQuery(id+"F0.wireOp",EDGE,"E10");Q44=makeQuery(id+"F2.opFillet","BLEND_EDGE",EDGE,{"blendedFrom":[makeQuery(id+"F1.opExtrude","SWEPT_EDGE",EDGE,{"disambiguationData":[OSD([subQ1,subQ0])]}),makeQuery(id+"F1.opExtrude","CAP_FACE",FACE,{"disambiguationData":[OSD([sQuery(id+"F0.wireOp",EDGE,"E0"),sQuery(id+"F0.wireOp",EDGE,"E1"),sQuery(id+"F0.wireOp",EDGE,"E2"),sQuery(id+"F0.wireOp",EDGE,"E3"),sQuery(id+"F0.wireOp",EDGE,"E4"),sQuery(id+"F0.wireOp",EDGE,"E5"),sQuery(id+"F0.wireOp",EDGE,"E6"),sQuery(id+"F0.wireOp",EDGE,"E7"),sQuery(id+"F0.wireOp",EDGE,"E8"),sQuery(id+"F0.wireOp",EDGE,"E9"),subQ1,subQ0])],"isStart":false})],"blendedInto":[makeQuery(id+"F1.opExtrude","CAP_FACE",FACE,{"disambiguationData":[OSD([sQuery(id+"F0.wireOp",EDGE,"E0"),sQuery(id+"F0.wireOp",EDGE,"E1"),sQuery(id+"F0.wireOp",EDGE,"E2"),sQuery(id+"F0.wireOp",EDGE,"E3"),sQuery(id+"F0.wireOp",EDGE,"E4"),sQuery(id+"F0.wireOp",EDGE,"E5"),sQuery(id+"F0.wireOp",EDGE,"E6"),sQuery(id+"F0.wireOp",EDGE,"E7"),sQuery(id+"F0.wireOp",EDGE,"E8"),sQuery(id+"F0.wireOp",EDGE,"E9"),subQ1,subQ0])],"isStart":false})]});}
            var Q45;
            Q45=makeQuery(id+"F1.opExtrude","CAP_EDGE",EDGE,{"disambiguationData":[OSD([sQuery(id+"F0.wireOp",EDGE,"E10")])],"isStart":false});
            var Q46;
            {var subQ0=sQuery(id+"F0.wireOp",EDGE,"E10");var subQ1=sQuery(id+"F0.wireOp",EDGE,"E9");Q46=makeQuery(id+"F2.opFillet","BLEND_EDGE",EDGE,{"blendedFrom":[makeQuery(id+"F1.opExtrude","SWEPT_EDGE",EDGE,{"disambiguationData":[OSD([subQ1,subQ0])]}),makeQuery(id+"F1.opExtrude","CAP_FACE",FACE,{"disambiguationData":[OSD([sQuery(id+"F0.wireOp",EDGE,"E0"),sQuery(id+"F0.wireOp",EDGE,"E1"),sQuery(id+"F0.wireOp",EDGE,"E2"),sQuery(id+"F0.wireOp",EDGE,"E3"),sQuery(id+"F0.wireOp",EDGE,"E4"),sQuery(id+"F0.wireOp",EDGE,"E5"),sQuery(id+"F0.wireOp",EDGE,"E6"),sQuery(id+"F0.wireOp",EDGE,"E7"),sQuery(id+"F0.wireOp",EDGE,"E8"),subQ1,subQ0,sQuery(id+"F0.wireOp",EDGE,"E11")])],"isStart":false})],"blendedInto":[makeQuery(id+"F1.opExtrude","CAP_FACE",FACE,{"disambiguationData":[OSD([sQuery(id+"F0.wireOp",EDGE,"E0"),sQuery(id+"F0.wireOp",EDGE,"E1"),sQuery(id+"F0.wireOp",EDGE,"E2"),sQuery(id+"F0.wireOp",EDGE,"E3"),sQuery(id+"F0.wireOp",EDGE,"E4"),sQuery(id+"F0.wireOp",EDGE,"E5"),sQuery(id+"F0.wireOp",EDGE,"E6"),sQuery(id+"F0.wireOp",EDGE,"E7"),sQuery(id+"F0.wireOp",EDGE,"E8"),subQ1,subQ0,sQuery(id+"F0.wireOp",EDGE,"E11")])],"isStart":false})]});}
            var Q47;
            Q47=makeQuery(id+"F1.opExtrude","CAP_EDGE",EDGE,{"disambiguationData":[OSD([sQuery(id+"F0.wireOp",EDGE,"E9")])],"isStart":false});
            var Q48;
            Q48=makeQuery(id+"F3.opFillet","BLEND_EDGE",EDGE,{"blendedFrom":[makeQuery(id+"F1.opExtrude","CAP_EDGE",EDGE,{"disambiguationData":[OSD([sQuery(id+"F0.wireOp",EDGE,"E8")])],"isStart":false}),makeQuery(id+"F1.opExtrude","SWEPT_FACE",FACE,{"disambiguationData":[OSD([sQuery(id+"F0.wireOp",EDGE,"E9")])]})],"blendedInto":[makeQuery(id+"F1.opExtrude","SWEPT_FACE",FACE,{"disambiguationData":[OSD([sQuery(id+"F0.wireOp",EDGE,"E9")])]})]});
            var Q49;
            {var subQ0=sQuery(id+"F0.wireOp",EDGE,"E8");Q49=makeQuery(id+"F3.opFillet","BLEND_EDGE",EDGE,{"blendedFrom":[makeQuery(id+"F1.opExtrude","CAP_EDGE",EDGE,{"disambiguationData":[OSD([subQ0])],"isStart":false}),makeQuery(id+"F2.opFillet","BLEND_FACE",FACE,{"disambiguationData":[OSD([subQ0,sQuery(id+"F0.wireOp",EDGE,"E9")])]})],"blendedInto":[makeQuery(id+"F2.opFillet","BLEND_FACE",FACE,{"disambiguationData":[OSD([subQ0,sQuery(id+"F0.wireOp",EDGE,"E9")])]})]});}
            var Q50;
            Q50=makeQuery(id+"F3.opFillet","BLEND_EDGE",EDGE,{"blendedFrom":[makeQuery(id+"F1.opExtrude","CAP_EDGE",EDGE,{"disambiguationData":[OSD([sQuery(id+"F0.wireOp",EDGE,"E4")])],"isStart":true}),makeQuery(id+"F1.opExtrude","SWEPT_FACE",FACE,{"disambiguationData":[OSD([sQuery(id+"F0.wireOp",EDGE,"E11")])]})],"blendedInto":[makeQuery(id+"F1.opExtrude","SWEPT_FACE",FACE,{"disambiguationData":[OSD([sQuery(id+"F0.wireOp",EDGE,"E11")])]})]});
            var Q51;
            {var subQ0=sQuery(id+"F0.wireOp",EDGE,"E4");Q51=makeQuery(id+"F3.opFillet","BLEND_EDGE",EDGE,{"blendedFrom":[makeQuery(id+"F1.opExtrude","CAP_EDGE",EDGE,{"disambiguationData":[OSD([subQ0])],"isStart":true}),makeQuery(id+"F2.opFillet","BLEND_FACE",FACE,{"disambiguationData":[OSD([subQ0,sQuery(id+"F0.wireOp",EDGE,"E11")])]})],"blendedInto":[makeQuery(id+"F2.opFillet","BLEND_FACE",FACE,{"disambiguationData":[OSD([subQ0,sQuery(id+"F0.wireOp",EDGE,"E11")])]})]});}
            var Q52;
            Q52=makeQuery(id+"F3.opFillet","BLEND_EDGE",EDGE,{"blendedFrom":[makeQuery(id+"F1.opExtrude","CAP_EDGE",EDGE,{"disambiguationData":[OSD([sQuery(id+"F0.wireOp",EDGE,"E4")])],"isStart":false}),makeQuery(id+"F1.opExtrude","SWEPT_FACE",FACE,{"disambiguationData":[OSD([sQuery(id+"F0.wireOp",EDGE,"E11")])]})],"blendedInto":[makeQuery(id+"F1.opExtrude","SWEPT_FACE",FACE,{"disambiguationData":[OSD([sQuery(id+"F0.wireOp",EDGE,"E11")])]})]});
            var Q53;
            {var subQ0=sQuery(id+"F0.wireOp",EDGE,"E4");Q53=makeQuery(id+"F3.opFillet","BLEND_EDGE",EDGE,{"blendedFrom":[makeQuery(id+"F1.opExtrude","CAP_EDGE",EDGE,{"disambiguationData":[OSD([subQ0])],"isStart":false}),makeQuery(id+"F2.opFillet","BLEND_FACE",FACE,{"disambiguationData":[OSD([subQ0,sQuery(id+"F0.wireOp",EDGE,"E11")])]})],"blendedInto":[makeQuery(id+"F2.opFillet","BLEND_FACE",FACE,{"disambiguationData":[OSD([subQ0,sQuery(id+"F0.wireOp",EDGE,"E11")])]})]});}
            fillet(context, id + "F4", {"entities" : qUnion([Q0, Q1, Q2, Q3, Q4, Q5, Q6, Q7, Q8, Q9, Q10, Q11, Q12, Q13, Q14, Q15, Q16, Q17, Q18, Q19, Q20, Q21, Q22, Q23, Q24, Q25, Q26, Q27, Q28, Q29, Q30, Q31, Q32, Q33, Q34, Q35, Q36, Q37, Q38, Q39, Q40, Q41, Q42, Q43, Q44, Q45, Q46, Q47, Q48, Q49, Q50, Q51, Q52, Q53]), "radius" : 0.5 * mm, "allowEdgeOverflow" : false});
        }
        {
            var Q0;
            Q0=makeQuery(id+"F1.opExtrude","SWEPT_FACE",FACE,{"disambiguationData":[OSD([sQuery(id+"F0.wireOp",EDGE,"E7")])]});
            var sketch = newSketch(context, id + "F5", { "sketchPlane" : qUnion([Q0])});
            skPoint(sketch, "E12.endSnap0", {"position": v(1, 2) * mm});
            skCircle(sketch, "E13", {"center": v(1.95, 2) * mm, "radius": 0.45 * mm});
            skSolve(sketch);
        }
        {
            var Q0;
            Q0=makeQuery(id+"F1.opExtrude","SWEPT_FACE",FACE,{"disambiguationData":[OSD([sQuery(id+"F0.wireOp",EDGE,"E5")])]});
            var sketch = newSketch(context, id + "F6", { "sketchPlane" : qUnion([Q0])});
            skCircle(sketch, "E14", {"center": v(12.05, 2) * mm, "radius": 0.45 * mm});
            skSolve(sketch);
        }
        {
            var Q0;
            Q0=makeQuery(id+"F6.imprint","IMPRINT",FACE,{"disambiguationData":[TD([[makeQuery(id+"F6.imprint","IMPRINT",EDGE,{"derivedFrom":sQuery(id+"F6.wireOp",EDGE,"E14")}),1.0]])]});
            extrude(context, id + "F7", {"entities" : qUnion([Q0]), "operationType" : NewBodyOperationType.ADD, "depth" : 5 * mm, "offsetDistance" : 25 * mm, "hasSecondDirection" : true, "secondDirectionOppositeDirection" : true, "secondDirectionDepth" : 28 * mm});
        }
        {
            var Q0;
            Q0=makeQuery(id+"F5.imprint","IMPRINT",FACE,{"disambiguationData":[TD([[makeQuery(id+"F5.imprint","IMPRINT",EDGE,{"derivedFrom":sQuery(id+"F5.wireOp",EDGE,"E13")}),1.0]])]});
            extrude(context, id + "F8", {"entities" : qUnion([Q0]), "operationType" : NewBodyOperationType.ADD, "depth" : 9.6 * mm, "offsetDistance" : 25 * mm, "hasSecondDirection" : true, "secondDirectionOppositeDirection" : true, "secondDirectionDepth" : 23.4 * mm});
        }
        {
            var Q0;
            Q0=makeQuery(id+"F1.opExtrude","CAP_FACE",FACE,{"disambiguationData":[OSD([sQuery(id+"F0.wireOp",EDGE,"E0"),sQuery(id+"F0.wireOp",EDGE,"E1"),sQuery(id+"F0.wireOp",EDGE,"E2"),sQuery(id+"F0.wireOp",EDGE,"E3"),sQuery(id+"F0.wireOp",EDGE,"E4"),sQuery(id+"F0.wireOp",EDGE,"E5"),sQuery(id+"F0.wireOp",EDGE,"E6"),sQuery(id+"F0.wireOp",EDGE,"E7"),sQuery(id+"F0.wireOp",EDGE,"E8"),sQuery(id+"F0.wireOp",EDGE,"E9"),sQuery(id+"F0.wireOp",EDGE,"E10"),sQuery(id+"F0.wireOp",EDGE,"E11")])],"isStart":false});
            var sketch = newSketch(context, id + "F9", { "sketchPlane" : qUnion([Q0])});
            skCircle(sketch, "E15", {"center": v(-8, -5.5) * mm, "radius": 2.5 * mm});
            skSolve(sketch);
        }
        {
            var Q0;
            Q0=makeQuery(id+"F9.imprint","IMPRINT",FACE,{"disambiguationData":[TD([[makeQuery(id+"F9.imprint","IMPRINT",EDGE,{"derivedFrom":sQuery(id+"F9.wireOp",EDGE,"E15")}),1.0]])]});
            extrude(context, id + "F10", {"entities" : qUnion([Q0]), "operationType" : NewBodyOperationType.REMOVE, "oppositeDirection" : true, "depth" : 3 * mm, "offsetDistance" : 25 * mm});
        }
    });
